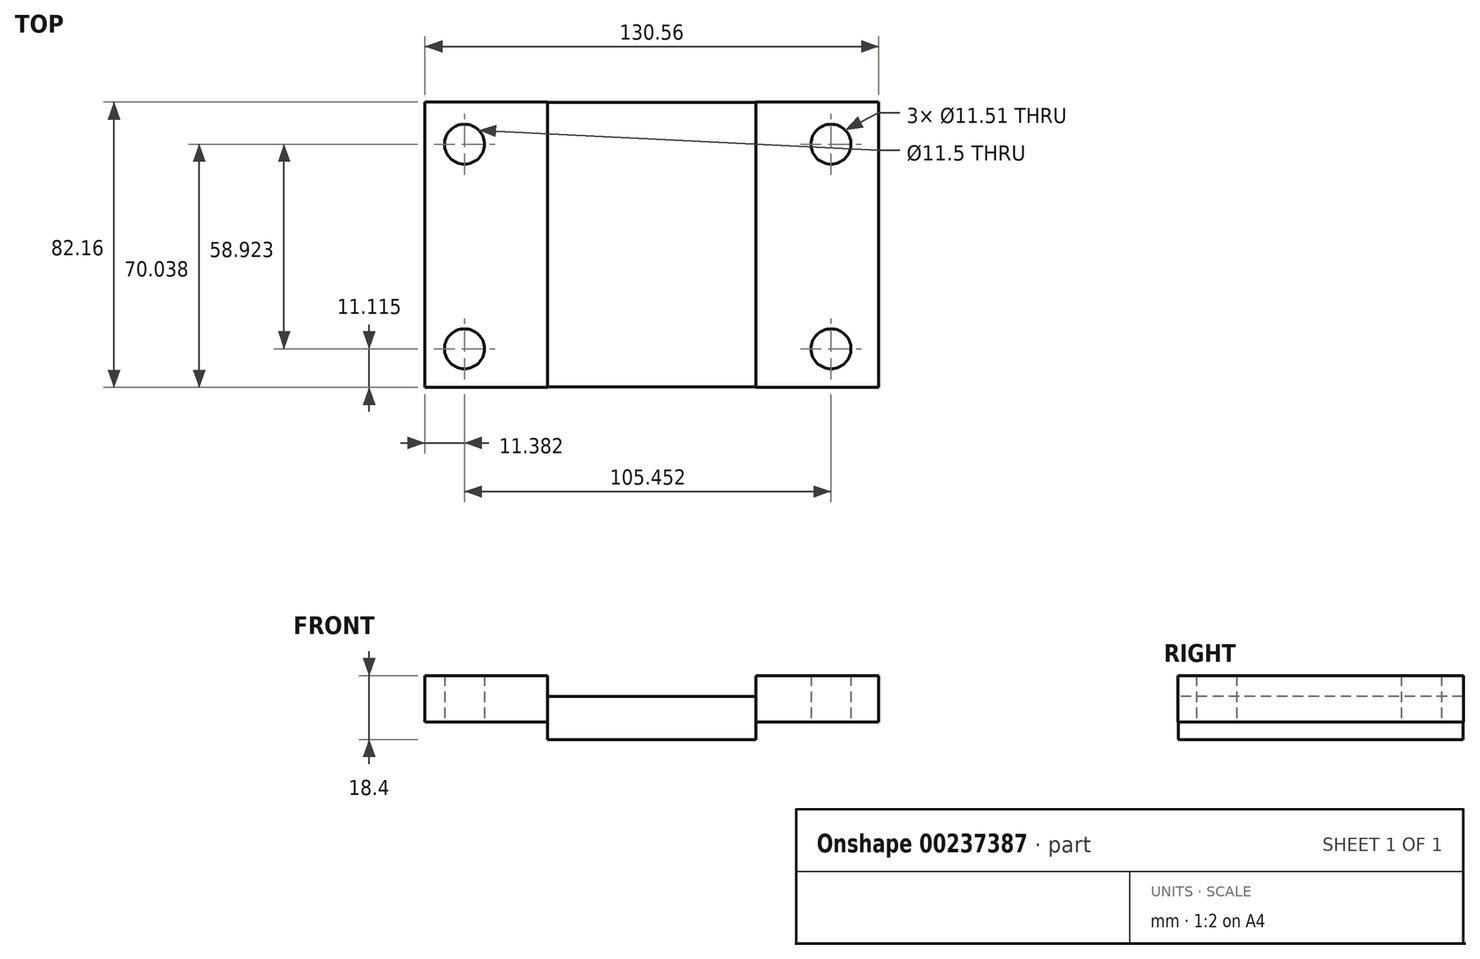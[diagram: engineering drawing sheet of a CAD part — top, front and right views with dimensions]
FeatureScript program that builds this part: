
annotation { "Feature Type Name" : "Feature", "Feature Type Description" : "" }
export const myFeature = defineFeature(function(context is Context, id is Id, definition is map)
    precondition{}
    {
        {
            var Q0;
            Q0=qCreatedBy(makeId("Top.planeOp"),FACE);
            var sketch = newSketch(context, id + "F0", { "sketchPlane" : qUnion([Q0])});
            skLineSegment(sketch, "E0.bottom", {"start": v(65.28, -41.08) * mm, "end": v(-65.28, -41.08) * mm});
            skLineSegment(sketch, "E0.top", {"start": v(65.28, 41.08) * mm, "end": v(-65.28, 41.08) * mm});
            skLineSegment(sketch, "E0.left", {"start": v(65.28, -41.08) * mm, "end": v(65.28, 41.08) * mm});
            skLineSegment(sketch, "E0.right", {"start": v(-65.28, -41.08) * mm, "end": v(-65.28, 41.08) * mm});
            skPoint(sketch, "E0.middle", {"position": v(0, 0) * mm});
            skLineSegment(sketch, "E1", {"start": v(-30, 41.08) * mm, "end": v(-30, -41.08) * mm});
            skLineSegment(sketch, "E2", {"start": v(30, 41.08) * mm, "end": v(30, -41.08) * mm});
            skCircle(sketch, "E3", {"center": v(-53.9, 28.96) * mm, "radius": 5.75 * mm});
            skCircle(sketch, "E4", {"center": v(-53.9, -29.96) * mm, "radius": 5.75 * mm});
            skCircle(sketch, "E5", {"center": v(51.55, -29.96) * mm, "radius": 5.75 * mm});
            skCircle(sketch, "E6", {"center": v(51.55, 28.96) * mm, "radius": 5.75 * mm});
            skSolve(sketch);
        }
        {
            var Q0;
            {var subQ1=sQuery(id+"F0.wireOp",EDGE,"E0.right");Q0=makeQuery(id+"F0.imprint","IMPRINT",FACE,{"disambiguationData":[TD([[makeQuery(id+"F0.imprint","IMPRINT",EDGE,{"derivedFrom":subQ1}),-1.0]])]});}
            var Q1;
            {var subQ1=sQuery(id+"F0.wireOp",EDGE,"E0.left");Q1=makeQuery(id+"F0.imprint","IMPRINT",FACE,{"disambiguationData":[TD([[makeQuery(id+"F0.imprint","IMPRINT",EDGE,{"derivedFrom":subQ1}),1.0]])]});}
            extrude(context, id + "F1", {"entities" : qUnion([Q0, Q1]), "depth" : 13.32 * mm});
        }
        {
            var Q0;
            Q0=qCreatedBy(makeId("Top.planeOp"),FACE);
            var sketch = newSketch(context, id + "F2", { "sketchPlane" : qUnion([Q0])});
            skLineSegment(sketch, "E7.bottom", {"start": v(29.97, 40.95) * mm, "end": v(-29.97, 40.95) * mm});
            skLineSegment(sketch, "E7.top", {"start": v(29.97, -40.95) * mm, "end": v(-29.97, -40.95) * mm});
            skLineSegment(sketch, "E7.left", {"start": v(29.97, 40.95) * mm, "end": v(29.97, -40.95) * mm});
            skLineSegment(sketch, "E7.right", {"start": v(-29.97, 40.95) * mm, "end": v(-29.97, -40.95) * mm});
            skPoint(sketch, "E7.middle", {"position": v(0, 0) * mm});
            skSolve(sketch);
        }
        {
            var Q0;
            Q0=makeQuery(id+"F2.imprint","IMPRINT",FACE,{"disambiguationData":[TD([[makeQuery(id+"F2.imprint","IMPRINT",EDGE,{"derivedFrom":sQuery(id+"F2.wireOp",EDGE,"E7.bottom")}),1.0]])]});
            extrude(context, id + "F3", {"entities" : qUnion([Q0]), "oppositeDirection" : true, "depth" : 5.08 * mm});
        }
        {
            var Q0;
            Q0=makeQuery(id+"F3.opExtrude","CAP_FACE",FACE,{"disambiguationData":[OSD([sQuery(id+"F2.wireOp",EDGE,"E7.bottom"),sQuery(id+"F2.wireOp",EDGE,"E7.top"),sQuery(id+"F2.wireOp",EDGE,"E7.left"),sQuery(id+"F2.wireOp",EDGE,"E7.right")])],"isStart":true});
            var sketch = newSketch(context, id + "F4", { "sketchPlane" : qUnion([Q0])});
            skLineSegment(sketch, "E8.bottom", {"start": v(29.97, 40.95) * mm, "end": v(-29.97, 40.95) * mm});
            skLineSegment(sketch, "E8.top", {"start": v(29.97, -40.95) * mm, "end": v(-29.97, -40.95) * mm});
            skLineSegment(sketch, "E8.left", {"start": v(29.97, 40.95) * mm, "end": v(29.97, -40.95) * mm});
            skLineSegment(sketch, "E8.right", {"start": v(-29.97, 40.95) * mm, "end": v(-29.97, -40.95) * mm});
            skPoint(sketch, "E8.middle", {"position": v(0, 0) * mm});
            skSolve(sketch);
        }
        {
            var Q0;
            Q0=makeQuery(id+"F4.imprint","IMPRINT",FACE,{"disambiguationData":[TD([[makeQuery(id+"F4.imprint","IMPRINT",EDGE,{"derivedFrom":sQuery(id+"F4.wireOp",EDGE,"E8.bottom")}),1.0]])]});
            extrude(context, id + "F5", {"entities" : qUnion([Q0]), "operationType" : NewBodyOperationType.ADD, "depth" : 7.37 * mm});
        }
    });
